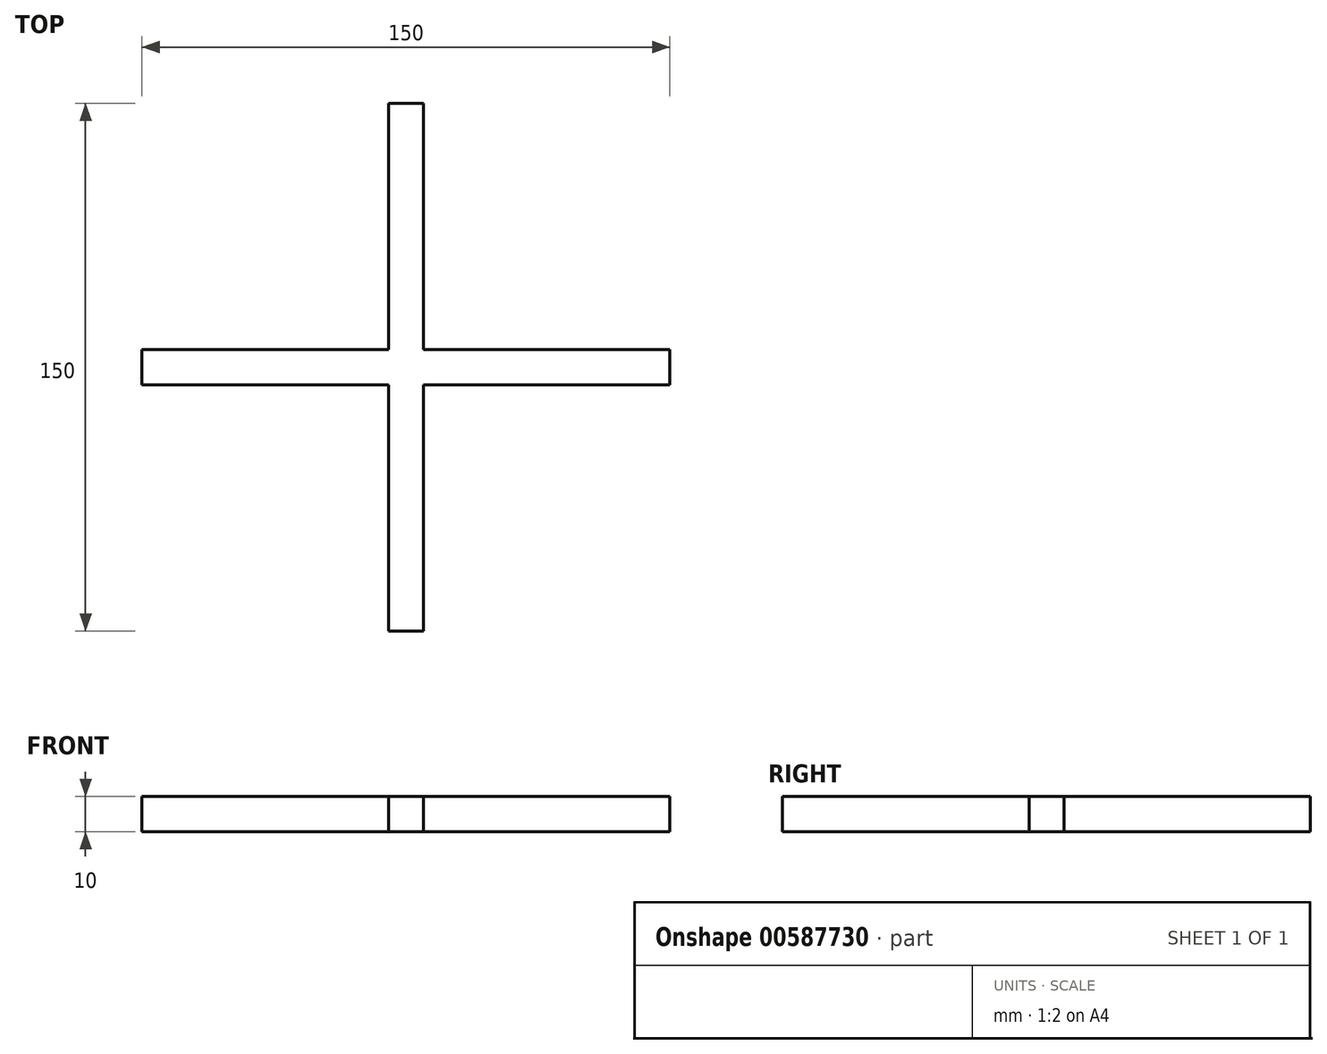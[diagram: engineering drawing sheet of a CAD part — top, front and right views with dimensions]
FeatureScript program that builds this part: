
annotation { "Feature Type Name" : "Feature", "Feature Type Description" : "" }
export const myFeature = defineFeature(function(context is Context, id is Id, definition is map)
    precondition{}
    {
        {
            var Q0;
            Q0=qCreatedBy(makeId("Top.planeOp"),FACE);
            var sketch = newSketch(context, id + "F0", { "sketchPlane" : qUnion([Q0])});
            skLineSegment(sketch, "E0.bottom", {"start": v(-5, 75) * mm, "end": v(5, 75) * mm});
            skLineSegment(sketch, "E0.top", {"start": v(-5, -75) * mm, "end": v(5, -75) * mm});
            skLineSegment(sketch, "E0.left", {"start": v(-5, 75) * mm, "end": v(-5, 5) * mm});
            skLineSegment(sketch, "E0.right", {"start": v(5, 75) * mm, "end": v(5, 5) * mm});
            skPoint(sketch, "E0.middle", {"position": v(0, 0) * mm});
            skLineSegment(sketch, "E1.bottom", {"start": v(-75, 5) * mm, "end": v(-5, 5) * mm});
            skLineSegment(sketch, "E1.top", {"start": v(-75, -5) * mm, "end": v(-5, -5) * mm});
            skLineSegment(sketch, "E1.left", {"start": v(-75, 5) * mm, "end": v(-75, -5) * mm});
            skLineSegment(sketch, "E1.right", {"start": v(75, 5) * mm, "end": v(75, -5) * mm});
            skLineSegment(sketch, "E2.trimOffspring", {"start": v(-5, -5) * mm, "end": v(-5, -75) * mm});
            skLineSegment(sketch, "E3.trimOffspring", {"start": v(5, 5) * mm, "end": v(75, 5) * mm});
            skLineSegment(sketch, "E4.trimOffspring", {"start": v(5, -5) * mm, "end": v(5, -75) * mm});
            skLineSegment(sketch, "E5.trimOffspring", {"start": v(5, -5) * mm, "end": v(75, -5) * mm});
            skSolve(sketch);
        }
        {
            var Q0;
            Q0=makeQuery(id+"F0.imprint","IMPRINT",FACE,{"disambiguationData":[TD([[makeQuery(id+"F0.imprint","IMPRINT",EDGE,{"derivedFrom":sQuery(id+"F0.wireOp",EDGE,"E0.bottom")}),-1.0]])]});
            extrude(context, id + "F1", {"entities" : qUnion([Q0]), "endBound" : BoundingType.SYMMETRIC, "depth" : 10 * mm, "offsetDistance" : 25 * mm});
        }
    });
